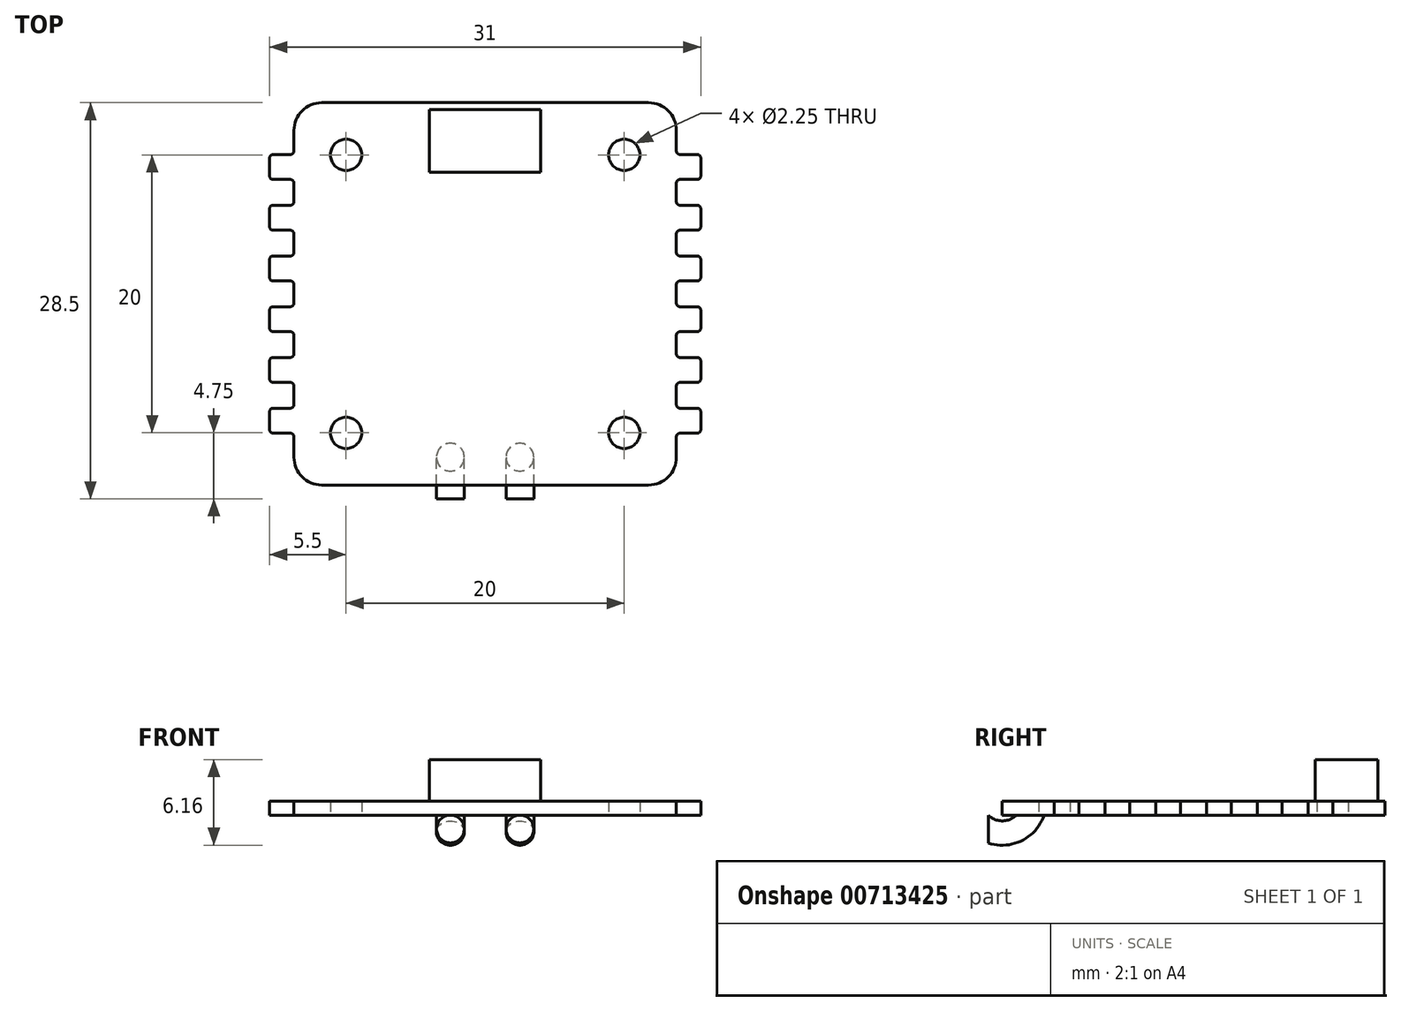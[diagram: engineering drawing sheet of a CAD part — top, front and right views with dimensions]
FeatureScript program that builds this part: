
annotation { "Feature Type Name" : "Feature", "Feature Type Description" : "" }
export const myFeature = defineFeature(function(context is Context, id is Id, definition is map)
    precondition{}
    {
        {
            var Q0;
            Q0=qCreatedBy(makeId("Top.planeOp"),FACE);
            var sketch = newSketch(context, id + "F0", { "sketchPlane" : qUnion([Q0])});
            skLineSegment(sketch, "E0.bottom", {"start": v(-11.75, 13.75) * mm, "end": v(11.75, 13.75) * mm});
            skLineSegment(sketch, "E0.top", {"start": v(-11.75, -13.75) * mm, "end": v(11.75, -13.75) * mm});
            skLineSegment(sketch, "E0.left", {"start": v(-13.75, 11.75) * mm, "end": v(-13.75, -11.75) * mm});
            skLineSegment(sketch, "E0.right", {"start": v(13.75, 11.75) * mm, "end": v(13.75, -11.75) * mm});
            skPoint(sketch, "E0.middle", {"position": v(0, 0) * mm});
            skCircle(sketch, "E1", {"center": v(-10, 10) * mm, "radius": 1.13 * mm});
            skCircle(sketch, "E2.MirrorC", {"center": v(10, 10) * mm, "radius": 1.13 * mm});
            skCircle(sketch, "E3.MirrorC", {"center": v(10, -10) * mm, "radius": 1.13 * mm});
            skCircle(sketch, "E4.MirrorC", {"center": v(-10, -10) * mm, "radius": 1.13 * mm});
            skPoint(sketch, "E5.visualSharp", {"position": v(-13.75, 13.75) * mm});
            skArc(sketch, "E5.filletArc", {"start": v(-11.75, 13.75) * mm, "mid": v(-13.16, 13.16) * mm, "end": v(-13.75, 11.75) * mm});
            skPoint(sketch, "E6.visualSharp", {"position": v(13.75, 13.75) * mm});
            skArc(sketch, "E6.filletArc", {"start": v(13.75, 11.75) * mm, "mid": v(13.16, 13.16) * mm, "end": v(11.75, 13.75) * mm});
            skPoint(sketch, "E7.visualSharp", {"position": v(13.75, -13.75) * mm});
            skArc(sketch, "E7.filletArc", {"start": v(11.75, -13.75) * mm, "mid": v(13.16, -13.16) * mm, "end": v(13.75, -11.75) * mm});
            skPoint(sketch, "E8.visualSharp", {"position": v(-13.75, -13.75) * mm});
            skArc(sketch, "E8.filletArc", {"start": v(-13.75, -11.75) * mm, "mid": v(-13.16, -13.16) * mm, "end": v(-11.75, -13.75) * mm});
            skLineSegment(sketch, "E9.bottom", {"start": v(-4, 13.25) * mm, "end": v(4, 13.25) * mm});
            skLineSegment(sketch, "E9.top", {"start": v(-4, 8.75) * mm, "end": v(4, 8.75) * mm});
            skLineSegment(sketch, "E9.left", {"start": v(-4, 13.25) * mm, "end": v(-4, 8.75) * mm});
            skLineSegment(sketch, "E9.right", {"start": v(4, 13.25) * mm, "end": v(4, 8.75) * mm});
            skPoint(sketch, "E9.middle", {"position": v(0, 11) * mm});
            skLineSegment(sketch, "E10.bottom", {"start": v(-13.75, 10.03) * mm, "end": v(-15.5, 10.03) * mm});
            skLineSegment(sketch, "E10.top", {"start": v(-13.75, 8.23) * mm, "end": v(-15.5, 8.23) * mm});
            skLineSegment(sketch, "E10.left", {"start": v(-13.75, 10.03) * mm, "end": v(-13.75, 8.23) * mm});
            skLineSegment(sketch, "E10.right", {"start": v(-15.5, 10.03) * mm, "end": v(-15.5, 8.23) * mm});
            skLineSegment(sketch, "E11.bottom", {"start": v(-13.75, 6.38) * mm, "end": v(-15.5, 6.38) * mm});
            skLineSegment(sketch, "E11.top", {"start": v(-13.75, 4.58) * mm, "end": v(-15.5, 4.58) * mm});
            skLineSegment(sketch, "E11.left", {"start": v(-13.75, 6.38) * mm, "end": v(-13.75, 4.58) * mm});
            skLineSegment(sketch, "E11.right", {"start": v(-15.5, 6.38) * mm, "end": v(-15.5, 4.58) * mm});
            skLineSegment(sketch, "E12.bottom", {"start": v(-13.75, 2.73) * mm, "end": v(-15.5, 2.73) * mm});
            skLineSegment(sketch, "E12.top", {"start": v(-13.75, 0.93) * mm, "end": v(-15.5, 0.93) * mm});
            skLineSegment(sketch, "E12.left", {"start": v(-13.75, 2.73) * mm, "end": v(-13.75, 0.92) * mm});
            skLineSegment(sketch, "E12.right", {"start": v(-15.5, 2.73) * mm, "end": v(-15.5, 0.93) * mm});
            skLineSegment(sketch, "E13", {"start": v(-13.75, 6.38) * mm, "end": v(-13.75, 8.23) * mm, "construction": true});
            skLineSegment(sketch, "E14", {"start": v(-13.75, 2.73) * mm, "end": v(-13.75, 4.58) * mm, "construction": true});
            skLineSegment(sketch, "E15.MirrorCS", {"start": v(-13.75, -2.73) * mm, "end": v(-13.75, -4.58) * mm, "construction": true});
            skLineSegment(sketch, "E16.MirrorCS", {"start": v(-13.75, -6.38) * mm, "end": v(-13.75, -4.58) * mm});
            skLineSegment(sketch, "E17.MirrorCS", {"start": v(-13.75, -6.38) * mm, "end": v(-13.75, -8.23) * mm, "construction": true});
            skLineSegment(sketch, "E18.MirrorCS", {"start": v(-13.75, -10.03) * mm, "end": v(-13.75, -8.23) * mm});
            skLineSegment(sketch, "E19.MirrorCS", {"start": v(-13.75, -8.23) * mm, "end": v(-15.5, -8.23) * mm});
            skLineSegment(sketch, "E20.MirrorCS", {"start": v(-13.75, -2.73) * mm, "end": v(-15.5, -2.73) * mm});
            skLineSegment(sketch, "E21.MirrorCS", {"start": v(-13.75, -4.58) * mm, "end": v(-15.5, -4.58) * mm});
            skLineSegment(sketch, "E22.MirrorCS", {"start": v(-15.5, -6.38) * mm, "end": v(-15.5, -4.58) * mm});
            skLineSegment(sketch, "E23.MirrorCS", {"start": v(-13.75, -6.38) * mm, "end": v(-15.5, -6.38) * mm});
            skLineSegment(sketch, "E24.MirrorCS", {"start": v(-13.75, -10.03) * mm, "end": v(-15.5, -10.03) * mm});
            skLineSegment(sketch, "E25.MirrorCS", {"start": v(-13.75, -0.92) * mm, "end": v(-15.5, -0.92) * mm});
            skLineSegment(sketch, "E26.MirrorCS", {"start": v(-15.5, -10.03) * mm, "end": v(-15.5, -8.23) * mm});
            skLineSegment(sketch, "E27.MirrorCS", {"start": v(-13.75, -2.73) * mm, "end": v(-13.75, -0.92) * mm});
            skLineSegment(sketch, "E28.MirrorCS", {"start": v(-15.5, -2.73) * mm, "end": v(-15.5, -0.93) * mm});
            skLineSegment(sketch, "E29.MirrorCS", {"start": v(13.75, 6.38) * mm, "end": v(13.75, 4.58) * mm});
            skLineSegment(sketch, "E30.MirrorCS", {"start": v(13.75, 2.73) * mm, "end": v(13.75, 4.58) * mm, "construction": true});
            skLineSegment(sketch, "E31.MirrorCS", {"start": v(13.75, -2.73) * mm, "end": v(13.75, -4.58) * mm, "construction": true});
            skLineSegment(sketch, "E32.MirrorCS", {"start": v(13.75, 6.38) * mm, "end": v(13.75, 8.23) * mm, "construction": true});
            skLineSegment(sketch, "E33.MirrorCS", {"start": v(13.75, -6.38) * mm, "end": v(13.75, -4.58) * mm});
            skLineSegment(sketch, "E34.MirrorCS", {"start": v(13.75, -6.38) * mm, "end": v(13.75, -8.23) * mm, "construction": true});
            skLineSegment(sketch, "E35.MirrorCS", {"start": v(13.75, 10.03) * mm, "end": v(13.75, 8.23) * mm});
            skLineSegment(sketch, "E36.MirrorCS", {"start": v(13.75, 8.22) * mm, "end": v(15.5, 8.22) * mm});
            skLineSegment(sketch, "E37.MirrorCS", {"start": v(15.5, 10.03) * mm, "end": v(15.5, 8.23) * mm});
            skLineSegment(sketch, "E38.MirrorCS", {"start": v(13.75, 10.02) * mm, "end": v(15.5, 10.02) * mm});
            skLineSegment(sketch, "E39.MirrorCS", {"start": v(13.75, 6.37) * mm, "end": v(15.5, 6.37) * mm});
            skLineSegment(sketch, "E40.MirrorCS", {"start": v(13.75, -4.58) * mm, "end": v(15.5, -4.58) * mm});
            skLineSegment(sketch, "E41.MirrorCS", {"start": v(13.75, 4.57) * mm, "end": v(15.5, 4.57) * mm});
            skLineSegment(sketch, "E42.MirrorCS", {"start": v(15.5, -6.38) * mm, "end": v(15.5, -4.58) * mm});
            skLineSegment(sketch, "E43.MirrorCS", {"start": v(13.75, -6.38) * mm, "end": v(15.5, -6.38) * mm});
            skLineSegment(sketch, "E44.MirrorCS", {"start": v(13.75, 2.72) * mm, "end": v(15.5, 2.72) * mm});
            skLineSegment(sketch, "E45.MirrorCS", {"start": v(13.75, -2.73) * mm, "end": v(13.75, -0.92) * mm});
            skLineSegment(sketch, "E46.MirrorCS", {"start": v(15.5, 6.38) * mm, "end": v(15.5, 4.58) * mm});
            skLineSegment(sketch, "E47.MirrorCS", {"start": v(13.75, -8.23) * mm, "end": v(15.5, -8.23) * mm});
            skLineSegment(sketch, "E48.MirrorCS", {"start": v(15.5, -2.73) * mm, "end": v(15.5, -0.93) * mm});
            skLineSegment(sketch, "E49.MirrorCS", {"start": v(13.75, -0.93) * mm, "end": v(15.5, -0.93) * mm});
            skLineSegment(sketch, "E50.MirrorCS", {"start": v(15.5, -10.03) * mm, "end": v(15.5, -8.23) * mm});
            skLineSegment(sketch, "E51.MirrorCS", {"start": v(15.5, 2.73) * mm, "end": v(15.5, 0.93) * mm});
            skLineSegment(sketch, "E52.MirrorCS", {"start": v(13.75, -2.73) * mm, "end": v(15.5, -2.73) * mm});
            skLineSegment(sketch, "E53.MirrorCS", {"start": v(13.75, 0.92) * mm, "end": v(15.5, 0.92) * mm});
            skLineSegment(sketch, "E54.MirrorCS", {"start": v(13.75, -10.03) * mm, "end": v(15.5, -10.03) * mm});
            skLineSegment(sketch, "E55.MirrorCS", {"start": v(13.75, -10.03) * mm, "end": v(13.75, -8.23) * mm});
            skLineSegment(sketch, "E56.MirrorCS", {"start": v(13.75, 2.73) * mm, "end": v(13.75, 0.92) * mm});
            skCircle(sketch, "E57", {"center": v(-2.5, -11.75) * mm, "radius": 1 * mm});
            skCircle(sketch, "E58", {"center": v(2.5, -11.75) * mm, "radius": 1 * mm});
            skLineSegment(sketch, "E59", {"start": v(-2.5, -11.75) * mm, "end": v(0, -11.75) * mm, "construction": true});
            skLineSegment(sketch, "E60", {"start": v(0, -11.75) * mm, "end": v(2.5, -11.75) * mm, "construction": true});
            skSolve(sketch);
        }
        {
            var Q0;
            Q0=makeQuery(id+"F0.imprint","IMPRINT",FACE,{"disambiguationData":[TD([[makeQuery(id+"F0.imprint","IMPRINT",EDGE,{"derivedFrom":sQuery(id+"F0.wireOp",EDGE,"E0.bottom")}),-1.0]])]});
            var Q1;
            Q1=makeQuery(id+"F0.imprint","IMPRINT",FACE,{"disambiguationData":[TD([[makeQuery(id+"F0.imprint","IMPRINT",EDGE,{"derivedFrom":sQuery(id+"F0.wireOp",EDGE,"E9.bottom")}),-1.0]])]});
            var Q2;
            {var subQ0=sQuery(id+"F0.wireOp",EDGE,"E10.bottom");Q2=makeQuery(id+"F0.imprint","IMPRINT",FACE,{"disambiguationData":[TD([[makeQuery(id+"F0.imprint","IMPRINT",EDGE,{"derivedFrom":subQ0}),1.0]])]});}
            var Q3;
            {var subQ0=sQuery(id+"F0.wireOp",EDGE,"E11.bottom");Q3=makeQuery(id+"F0.imprint","IMPRINT",FACE,{"disambiguationData":[TD([[makeQuery(id+"F0.imprint","IMPRINT",EDGE,{"derivedFrom":subQ0}),1.0]])]});}
            var Q4;
            {var subQ0=sQuery(id+"F0.wireOp",EDGE,"E12.bottom");Q4=makeQuery(id+"F0.imprint","IMPRINT",FACE,{"disambiguationData":[TD([[makeQuery(id+"F0.imprint","IMPRINT",EDGE,{"derivedFrom":subQ0}),1.0]])]});}
            var Q5;
            {var subQ0=sQuery(id+"F0.wireOp",EDGE,"E20.MirrorCS");Q5=makeQuery(id+"F0.imprint","IMPRINT",FACE,{"disambiguationData":[TD([[makeQuery(id+"F0.imprint","IMPRINT",EDGE,{"derivedFrom":subQ0}),-1.0]])]});}
            var Q6;
            {var subQ2=sQuery(id+"F0.wireOp",EDGE,"E21.MirrorCS");Q6=makeQuery(id+"F0.imprint","IMPRINT",FACE,{"disambiguationData":[TD([[makeQuery(id+"F0.imprint","IMPRINT",EDGE,{"derivedFrom":subQ2}),1.0]])]});}
            var Q7;
            {var subQ0=sQuery(id+"F0.wireOp",EDGE,"E19.MirrorCS");Q7=makeQuery(id+"F0.imprint","IMPRINT",FACE,{"disambiguationData":[TD([[makeQuery(id+"F0.imprint","IMPRINT",EDGE,{"derivedFrom":subQ0}),1.0]])]});}
            var Q8;
            {var subQ0=sQuery(id+"F0.wireOp",EDGE,"E47.MirrorCS");Q8=makeQuery(id+"F0.imprint","IMPRINT",FACE,{"disambiguationData":[TD([[makeQuery(id+"F0.imprint","IMPRINT",EDGE,{"derivedFrom":subQ0}),-1.0]])]});}
            var Q9;
            {var subQ0=sQuery(id+"F0.wireOp",EDGE,"E40.MirrorCS");Q9=makeQuery(id+"F0.imprint","IMPRINT",FACE,{"disambiguationData":[TD([[makeQuery(id+"F0.imprint","IMPRINT",EDGE,{"derivedFrom":subQ0}),-1.0]])]});}
            var Q10;
            Q10=makeQuery(id+"F0.imprint","IMPRINT",FACE,{"disambiguationData":[TD([[makeQuery(id+"F0.imprint","IMPRINT",EDGE,{"derivedFrom":sQuery(id+"F0.wireOp",EDGE,"E48.MirrorCS")}),1.0]])]});
            var Q11;
            {var subQ2=sQuery(id+"F0.wireOp",EDGE,"E44.MirrorCS");Q11=makeQuery(id+"F0.imprint","IMPRINT",FACE,{"disambiguationData":[TD([[makeQuery(id+"F0.imprint","IMPRINT",EDGE,{"derivedFrom":subQ2}),-1.0]])]});}
            var Q12;
            {var subQ0=sQuery(id+"F0.wireOp",EDGE,"E39.MirrorCS");Q12=makeQuery(id+"F0.imprint","IMPRINT",FACE,{"disambiguationData":[TD([[makeQuery(id+"F0.imprint","IMPRINT",EDGE,{"derivedFrom":subQ0}),-1.0]])]});}
            var Q13;
            {var subQ0=sQuery(id+"F0.wireOp",EDGE,"E36.MirrorCS");Q13=makeQuery(id+"F0.imprint","IMPRINT",FACE,{"disambiguationData":[TD([[makeQuery(id+"F0.imprint","IMPRINT",EDGE,{"derivedFrom":subQ0}),1.0]])]});}
            var Q14;
            Q14=makeQuery(id+"F0.imprint","IMPRINT",FACE,{"disambiguationData":[TD([[makeQuery(id+"F0.imprint","IMPRINT",EDGE,{"derivedFrom":sQuery(id+"F0.wireOp",EDGE,"E57")}),1.0]])]});
            var Q15;
            Q15=makeQuery(id+"F0.imprint","IMPRINT",FACE,{"disambiguationData":[TD([[makeQuery(id+"F0.imprint","IMPRINT",EDGE,{"derivedFrom":sQuery(id+"F0.wireOp",EDGE,"E58")}),1.0]])]});
            extrude(context, id + "F1", {"entities" : qUnion([Q0, Q1, Q2, Q3, Q4, Q5, Q6, Q7, Q8, Q9, Q10, Q11, Q12, Q13, Q14, Q15]), "depth" : 1 * mm, "offsetDistance" : 25 * mm});
        }
        {
            var Q0;
            Q0=makeQuery(id+"F0.imprint","IMPRINT",FACE,{"disambiguationData":[TD([[makeQuery(id+"F0.imprint","IMPRINT",EDGE,{"derivedFrom":sQuery(id+"F0.wireOp",EDGE,"E9.bottom")}),-1.0]])]});
            extrude(context, id + "F2", {"entities" : qUnion([Q0]), "depth" : 4 * mm, "offsetDistance" : 25 * mm, "hasSecondDirection" : true, "secondDirectionOppositeDirection" : false, "secondDirectionDepth" : 1 * mm});
        }
        {
            var Q0;
            Q0=makeQuery(id+"F1.opExtrude","SWEPT_EDGE",EDGE,{"disambiguationData":[OSD([sQuery(id+"F0.wireOp",EDGE,"E0.left"),sQuery(id+"F0.wireOp",EDGE,"E10.top")])]});
            var Q1;
            Q1=makeQuery(id+"F1.opExtrude","SWEPT_EDGE",EDGE,{"disambiguationData":[OSD([sQuery(id+"F0.wireOp",EDGE,"E0.left"),sQuery(id+"F0.wireOp",EDGE,"E11.bottom")])]});
            var Q2;
            Q2=makeQuery(id+"F1.opExtrude","SWEPT_EDGE",EDGE,{"disambiguationData":[OSD([sQuery(id+"F0.wireOp",EDGE,"E0.left"),sQuery(id+"F0.wireOp",EDGE,"E10.bottom")])]});
            var Q3;
            Q3=makeQuery(id+"F1.opExtrude","SWEPT_EDGE",EDGE,{"disambiguationData":[OSD([sQuery(id+"F0.wireOp",EDGE,"E0.left"),sQuery(id+"F0.wireOp",EDGE,"E12.bottom")])]});
            var Q4;
            Q4=makeQuery(id+"F1.opExtrude","SWEPT_EDGE",EDGE,{"disambiguationData":[OSD([sQuery(id+"F0.wireOp",EDGE,"E0.left"),sQuery(id+"F0.wireOp",EDGE,"E11.top")])]});
            var Q5;
            Q5=makeQuery(id+"F1.opExtrude","SWEPT_EDGE",EDGE,{"disambiguationData":[OSD([sQuery(id+"F0.wireOp",EDGE,"E0.left"),sQuery(id+"F0.wireOp",EDGE,"E12.top")])]});
            var Q6;
            Q6=makeQuery(id+"F1.opExtrude","SWEPT_EDGE",EDGE,{"disambiguationData":[OSD([sQuery(id+"F0.wireOp",EDGE,"E0.left"),sQuery(id+"F0.wireOp",EDGE,"E20.MirrorCS")])]});
            var Q7;
            Q7=makeQuery(id+"F1.opExtrude","SWEPT_EDGE",EDGE,{"disambiguationData":[OSD([sQuery(id+"F0.wireOp",EDGE,"E0.left"),sQuery(id+"F0.wireOp",EDGE,"E25.MirrorCS")])]});
            var Q8;
            Q8=makeQuery(id+"F1.opExtrude","SWEPT_EDGE",EDGE,{"disambiguationData":[OSD([sQuery(id+"F0.wireOp",EDGE,"E0.left"),sQuery(id+"F0.wireOp",EDGE,"E21.MirrorCS")])]});
            var Q9;
            Q9=makeQuery(id+"F1.opExtrude","SWEPT_EDGE",EDGE,{"disambiguationData":[OSD([sQuery(id+"F0.wireOp",EDGE,"E0.left"),sQuery(id+"F0.wireOp",EDGE,"E23.MirrorCS")])]});
            var Q10;
            Q10=makeQuery(id+"F1.opExtrude","SWEPT_EDGE",EDGE,{"disambiguationData":[OSD([sQuery(id+"F0.wireOp",EDGE,"E0.left"),sQuery(id+"F0.wireOp",EDGE,"E24.MirrorCS")])]});
            var Q11;
            Q11=makeQuery(id+"F1.opExtrude","SWEPT_EDGE",EDGE,{"disambiguationData":[OSD([sQuery(id+"F0.wireOp",EDGE,"E0.left"),sQuery(id+"F0.wireOp",EDGE,"E19.MirrorCS")])]});
            var Q12;
            Q12=makeQuery(id+"F1.opExtrude","SWEPT_EDGE",EDGE,{"disambiguationData":[OSD([sQuery(id+"F0.wireOp",EDGE,"E0.right"),sQuery(id+"F0.wireOp",EDGE,"E43.MirrorCS")])]});
            var Q13;
            Q13=makeQuery(id+"F1.opExtrude","SWEPT_EDGE",EDGE,{"disambiguationData":[OSD([sQuery(id+"F0.wireOp",EDGE,"E0.right"),sQuery(id+"F0.wireOp",EDGE,"E54.MirrorCS")])]});
            var Q14;
            Q14=makeQuery(id+"F1.opExtrude","SWEPT_EDGE",EDGE,{"disambiguationData":[OSD([sQuery(id+"F0.wireOp",EDGE,"E0.right"),sQuery(id+"F0.wireOp",EDGE,"E52.MirrorCS")])]});
            var Q15;
            Q15=makeQuery(id+"F1.opExtrude","SWEPT_EDGE",EDGE,{"disambiguationData":[OSD([sQuery(id+"F0.wireOp",EDGE,"E0.right"),sQuery(id+"F0.wireOp",EDGE,"E53.MirrorCS")])]});
            var Q16;
            Q16=makeQuery(id+"F1.opExtrude","SWEPT_EDGE",EDGE,{"disambiguationData":[OSD([sQuery(id+"F0.wireOp",EDGE,"E0.right"),sQuery(id+"F0.wireOp",EDGE,"E41.MirrorCS")])]});
            var Q17;
            Q17=makeQuery(id+"F1.opExtrude","SWEPT_EDGE",EDGE,{"disambiguationData":[OSD([sQuery(id+"F0.wireOp",EDGE,"E0.right"),sQuery(id+"F0.wireOp",EDGE,"E36.MirrorCS")])]});
            var Q18;
            Q18=makeQuery(id+"F1.opExtrude","SWEPT_EDGE",EDGE,{"disambiguationData":[OSD([sQuery(id+"F0.wireOp",EDGE,"E0.right"),sQuery(id+"F0.wireOp",EDGE,"E38.MirrorCS")])]});
            var Q19;
            Q19=makeQuery(id+"F1.opExtrude","SWEPT_EDGE",EDGE,{"disambiguationData":[OSD([sQuery(id+"F0.wireOp",EDGE,"E0.right"),sQuery(id+"F0.wireOp",EDGE,"E39.MirrorCS")])]});
            var Q20;
            Q20=makeQuery(id+"F1.opExtrude","SWEPT_EDGE",EDGE,{"disambiguationData":[OSD([sQuery(id+"F0.wireOp",EDGE,"E0.right"),sQuery(id+"F0.wireOp",EDGE,"E44.MirrorCS")])]});
            var Q21;
            Q21=makeQuery(id+"F1.opExtrude","SWEPT_EDGE",EDGE,{"disambiguationData":[OSD([sQuery(id+"F0.wireOp",EDGE,"E0.right"),sQuery(id+"F0.wireOp",EDGE,"E49.MirrorCS")])]});
            var Q22;
            Q22=makeQuery(id+"F1.opExtrude","SWEPT_EDGE",EDGE,{"disambiguationData":[OSD([sQuery(id+"F0.wireOp",EDGE,"E0.right"),sQuery(id+"F0.wireOp",EDGE,"E40.MirrorCS")])]});
            var Q23;
            Q23=makeQuery(id+"F1.opExtrude","SWEPT_EDGE",EDGE,{"disambiguationData":[OSD([sQuery(id+"F0.wireOp",EDGE,"E0.right"),sQuery(id+"F0.wireOp",EDGE,"E47.MirrorCS")])]});
            var Q24;
            Q24=makeQuery(id+"F1.opExtrude","SWEPT_EDGE",EDGE,{"disambiguationData":[OSD([sQuery(id+"F0.wireOp",EDGE,"E24.MirrorCS"),sQuery(id+"F0.wireOp",EDGE,"E26.MirrorCS")])]});
            var Q25;
            Q25=makeQuery(id+"F1.opExtrude","SWEPT_EDGE",EDGE,{"disambiguationData":[OSD([sQuery(id+"F0.wireOp",EDGE,"E19.MirrorCS"),sQuery(id+"F0.wireOp",EDGE,"E26.MirrorCS")])]});
            var Q26;
            Q26=makeQuery(id+"F1.opExtrude","SWEPT_EDGE",EDGE,{"disambiguationData":[OSD([sQuery(id+"F0.wireOp",EDGE,"E22.MirrorCS"),sQuery(id+"F0.wireOp",EDGE,"E23.MirrorCS")])]});
            var Q27;
            Q27=makeQuery(id+"F1.opExtrude","SWEPT_EDGE",EDGE,{"disambiguationData":[OSD([sQuery(id+"F0.wireOp",EDGE,"E21.MirrorCS"),sQuery(id+"F0.wireOp",EDGE,"E22.MirrorCS")])]});
            var Q28;
            Q28=makeQuery(id+"F1.opExtrude","SWEPT_EDGE",EDGE,{"disambiguationData":[OSD([sQuery(id+"F0.wireOp",EDGE,"E20.MirrorCS"),sQuery(id+"F0.wireOp",EDGE,"E28.MirrorCS")])]});
            var Q29;
            Q29=makeQuery(id+"F1.opExtrude","SWEPT_EDGE",EDGE,{"disambiguationData":[OSD([sQuery(id+"F0.wireOp",EDGE,"E25.MirrorCS"),sQuery(id+"F0.wireOp",EDGE,"E28.MirrorCS")])]});
            var Q30;
            Q30=makeQuery(id+"F1.opExtrude","SWEPT_EDGE",EDGE,{"disambiguationData":[OSD([sQuery(id+"F0.wireOp",EDGE,"E12.top"),sQuery(id+"F0.wireOp",EDGE,"E12.right")])]});
            var Q31;
            Q31=makeQuery(id+"F1.opExtrude","SWEPT_EDGE",EDGE,{"disambiguationData":[OSD([sQuery(id+"F0.wireOp",EDGE,"E12.bottom"),sQuery(id+"F0.wireOp",EDGE,"E12.right")])]});
            var Q32;
            Q32=makeQuery(id+"F1.opExtrude","SWEPT_EDGE",EDGE,{"disambiguationData":[OSD([sQuery(id+"F0.wireOp",EDGE,"E11.top"),sQuery(id+"F0.wireOp",EDGE,"E11.right")])]});
            var Q33;
            Q33=makeQuery(id+"F1.opExtrude","SWEPT_EDGE",EDGE,{"disambiguationData":[OSD([sQuery(id+"F0.wireOp",EDGE,"E11.bottom"),sQuery(id+"F0.wireOp",EDGE,"E11.right")])]});
            var Q34;
            Q34=makeQuery(id+"F1.opExtrude","SWEPT_EDGE",EDGE,{"disambiguationData":[OSD([sQuery(id+"F0.wireOp",EDGE,"E10.top"),sQuery(id+"F0.wireOp",EDGE,"E10.right")])]});
            var Q35;
            Q35=makeQuery(id+"F1.opExtrude","SWEPT_EDGE",EDGE,{"disambiguationData":[OSD([sQuery(id+"F0.wireOp",EDGE,"E10.bottom"),sQuery(id+"F0.wireOp",EDGE,"E10.right")])]});
            var Q36;
            Q36=makeQuery(id+"F1.opExtrude","SWEPT_EDGE",EDGE,{"disambiguationData":[OSD([sQuery(id+"F0.wireOp",EDGE,"E50.MirrorCS"),sQuery(id+"F0.wireOp",EDGE,"E54.MirrorCS")])]});
            var Q37;
            Q37=makeQuery(id+"F1.opExtrude","SWEPT_EDGE",EDGE,{"disambiguationData":[OSD([sQuery(id+"F0.wireOp",EDGE,"E47.MirrorCS"),sQuery(id+"F0.wireOp",EDGE,"E50.MirrorCS")])]});
            var Q38;
            Q38=makeQuery(id+"F1.opExtrude","SWEPT_EDGE",EDGE,{"disambiguationData":[OSD([sQuery(id+"F0.wireOp",EDGE,"E42.MirrorCS"),sQuery(id+"F0.wireOp",EDGE,"E43.MirrorCS")])]});
            var Q39;
            Q39=makeQuery(id+"F1.opExtrude","SWEPT_EDGE",EDGE,{"disambiguationData":[OSD([sQuery(id+"F0.wireOp",EDGE,"E40.MirrorCS"),sQuery(id+"F0.wireOp",EDGE,"E42.MirrorCS")])]});
            var Q40;
            Q40=makeQuery(id+"F1.opExtrude","SWEPT_EDGE",EDGE,{"disambiguationData":[OSD([sQuery(id+"F0.wireOp",EDGE,"E48.MirrorCS"),sQuery(id+"F0.wireOp",EDGE,"E52.MirrorCS")])]});
            var Q41;
            Q41=makeQuery(id+"F1.opExtrude","SWEPT_EDGE",EDGE,{"disambiguationData":[OSD([sQuery(id+"F0.wireOp",EDGE,"E48.MirrorCS"),sQuery(id+"F0.wireOp",EDGE,"E49.MirrorCS")])]});
            var Q42;
            Q42=makeQuery(id+"F1.opExtrude","SWEPT_EDGE",EDGE,{"disambiguationData":[OSD([sQuery(id+"F0.wireOp",EDGE,"E51.MirrorCS"),sQuery(id+"F0.wireOp",EDGE,"E53.MirrorCS")])]});
            var Q43;
            Q43=makeQuery(id+"F1.opExtrude","SWEPT_EDGE",EDGE,{"disambiguationData":[OSD([sQuery(id+"F0.wireOp",EDGE,"E44.MirrorCS"),sQuery(id+"F0.wireOp",EDGE,"E51.MirrorCS")])]});
            var Q44;
            Q44=makeQuery(id+"F1.opExtrude","SWEPT_EDGE",EDGE,{"disambiguationData":[OSD([sQuery(id+"F0.wireOp",EDGE,"E41.MirrorCS"),sQuery(id+"F0.wireOp",EDGE,"E46.MirrorCS")])]});
            var Q45;
            Q45=makeQuery(id+"F1.opExtrude","SWEPT_EDGE",EDGE,{"disambiguationData":[OSD([sQuery(id+"F0.wireOp",EDGE,"E39.MirrorCS"),sQuery(id+"F0.wireOp",EDGE,"E46.MirrorCS")])]});
            var Q46;
            Q46=makeQuery(id+"F1.opExtrude","SWEPT_EDGE",EDGE,{"disambiguationData":[OSD([sQuery(id+"F0.wireOp",EDGE,"E36.MirrorCS"),sQuery(id+"F0.wireOp",EDGE,"E37.MirrorCS")])]});
            var Q47;
            Q47=makeQuery(id+"F1.opExtrude","SWEPT_EDGE",EDGE,{"disambiguationData":[OSD([sQuery(id+"F0.wireOp",EDGE,"E37.MirrorCS"),sQuery(id+"F0.wireOp",EDGE,"E38.MirrorCS")])]});
            fillet(context, id + "F3", {"entities" : qUnion([Q0, Q1, Q2, Q3, Q4, Q5, Q6, Q7, Q8, Q9, Q10, Q11, Q12, Q13, Q14, Q15, Q16, Q17, Q18, Q19, Q20, Q21, Q22, Q23, Q24, Q25, Q26, Q27, Q28, Q29, Q30, Q31, Q32, Q33, Q34, Q35, Q36, Q37, Q38, Q39, Q40, Q41, Q42, Q43, Q44, Q45, Q46, Q47]), "radius" : .25 * mm, "tangentPropagation" : true, "allowEdgeOverflow" : false});
        }
        {
            var Q0;
            Q0=makeQuery(id+"F0.imprint","IMPRINT",FACE,{"disambiguationData":[TD([[makeQuery(id+"F0.imprint","IMPRINT",EDGE,{"derivedFrom":sQuery(id+"F0.wireOp",EDGE,"E57")}),1.0]])]});
            var Q1;
            Q1=makeQuery(id+"F0.imprint","IMPRINT",FACE,{"disambiguationData":[TD([[makeQuery(id+"F0.imprint","IMPRINT",EDGE,{"derivedFrom":sQuery(id+"F0.wireOp",EDGE,"E58")}),1.0]])]});
            var Q2;
            Q2=makeQuery(id+"F1.opExtrude","CAP_EDGE",EDGE,{"disambiguationData":[OSD([sQuery(id+"F0.wireOp",EDGE,"E0.top")])],"isStart":false});
            revolve(context, id + "F4", {"surfaceOperationType" : NewSurfaceOperationType.NEW, "entities" : qUnion([Q0, Q1]), "axis" : qUnion([Q2]), "revolveType" : RevolveType.ONE_DIRECTION, "oppositeDirection" : true, "angle" : 90 * degree});
        }
    });
